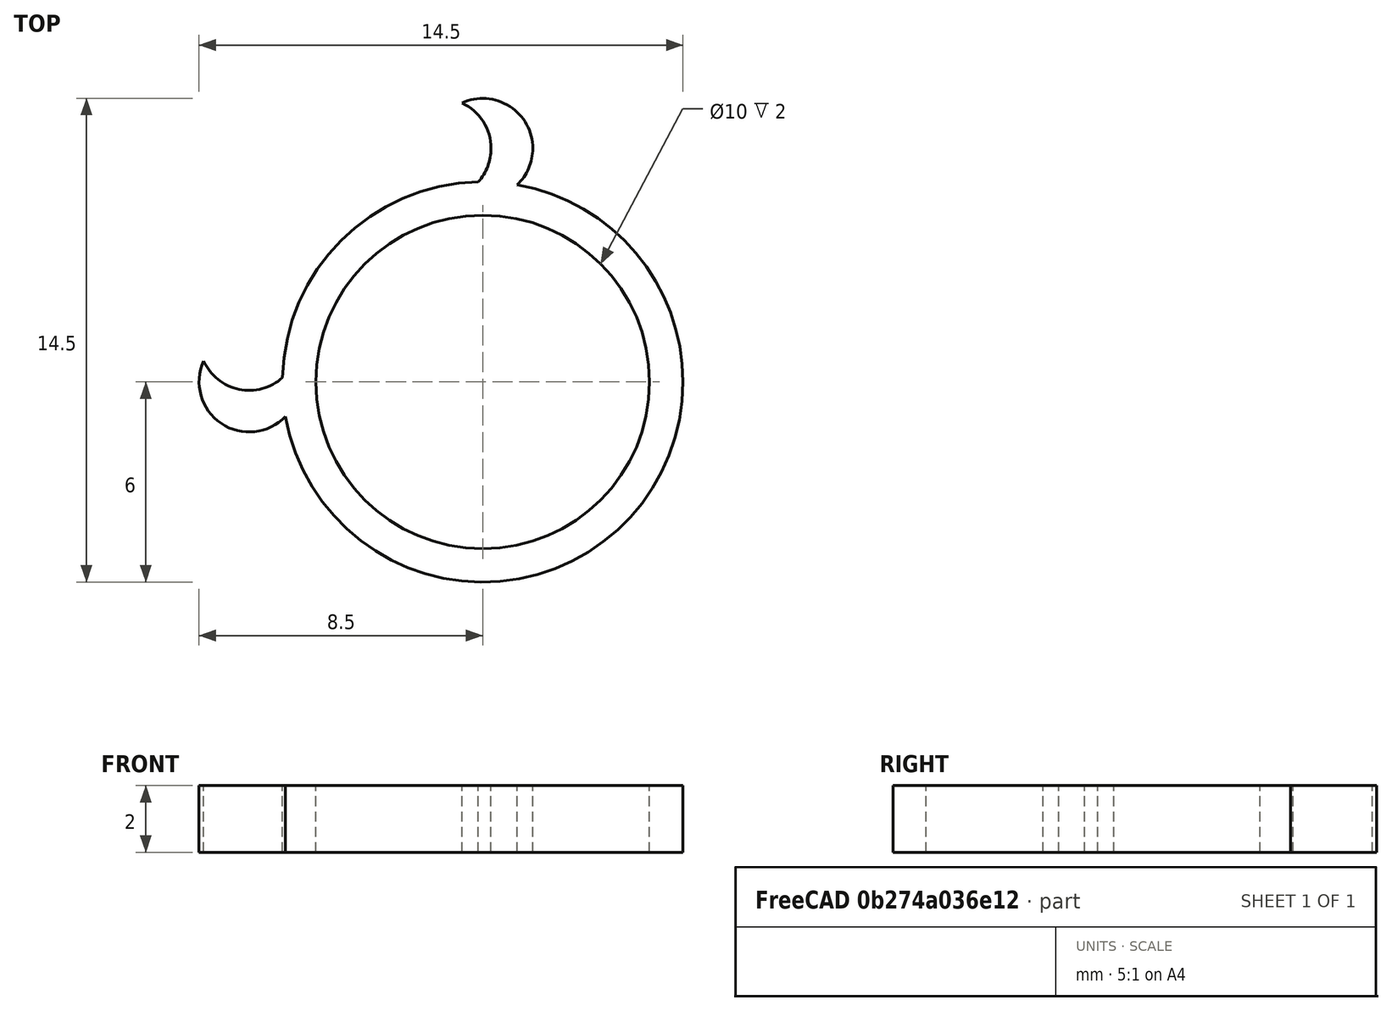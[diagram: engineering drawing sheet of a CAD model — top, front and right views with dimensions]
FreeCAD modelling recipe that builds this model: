
FCSTD DOCUMENT  (FreeCAD 0.19R24291 (Git))
Label: reto7
License: All rights reserved
LicenseURL: http://en.wikipedia.org/wiki/All_rights_reserved
objects: Part::Cylinder×6, Part::MultiFuse×3, Part::Cut×2
note: 11 computed .brp shape members not serialized (recipe doc carries the construction recipe); baked Part::Feature solids carry a one-line shape summary decoded from their .brp

FEATURE [Part::Cylinder] Cylinder
  Angle = 360
  AttacherType = Attacher::AttachEngine3D
  Height = 2
  Radius = 6
FEATURE [Part::Cylinder] Cylinder001
  Angle = 360
  AttacherType = Attacher::AttachEngine3D
  Height = 3
  Radius = 5
FEATURE [Part::Cut] Cut
  Base = -> Cylinder
  Refine = true
  Tool = -> Cylinder001
FEATURE [Part::Cylinder] Cylinder002
  Angle = 360
  AttacherType = Attacher::AttachEngine3D
  Height = 2
  Placement = pos=(-7,0,0) rot=(0,0,1;0rad)
  Radius = 1.5
FEATURE [Part::Cylinder] Cylinder003
  Angle = 360
  AttacherType = Attacher::AttachEngine3D
  Height = 2
  Placement = pos=(0,7,0) rot=(0,0,1;0rad)
  Radius = 1.5
FEATURE [Part::Cylinder] Cylinder004
  Angle = 360
  AttacherType = Attacher::AttachEngine3D
  Height = 10
  Placement = pos=(-7,1.25,0) rot=(0,0,1;0rad)
  Radius = 1.5
FEATURE [Part::Cylinder] Cylinder005
  Angle = 360
  AttacherType = Attacher::AttachEngine3D
  Height = 10
  Placement = pos=(-1.25,7,0) rot=(0,0,1;0rad)
  Radius = 1.5
FEATURE [Part::MultiFuse] Fusion
  Refine = true
  Shapes = -> [Cylinder004,Cylinder005]
FEATURE [Part::MultiFuse] Fusion001
  Refine = true
  Shapes = -> [Cylinder002,Cylinder003]
FEATURE [Part::Cut] Cut001
  Base = -> Fusion001
  Refine = true
  Tool = -> Fusion
FEATURE [Part::MultiFuse] Fusion002
  Refine = true
  Shapes = -> [Cut001,Cut]
